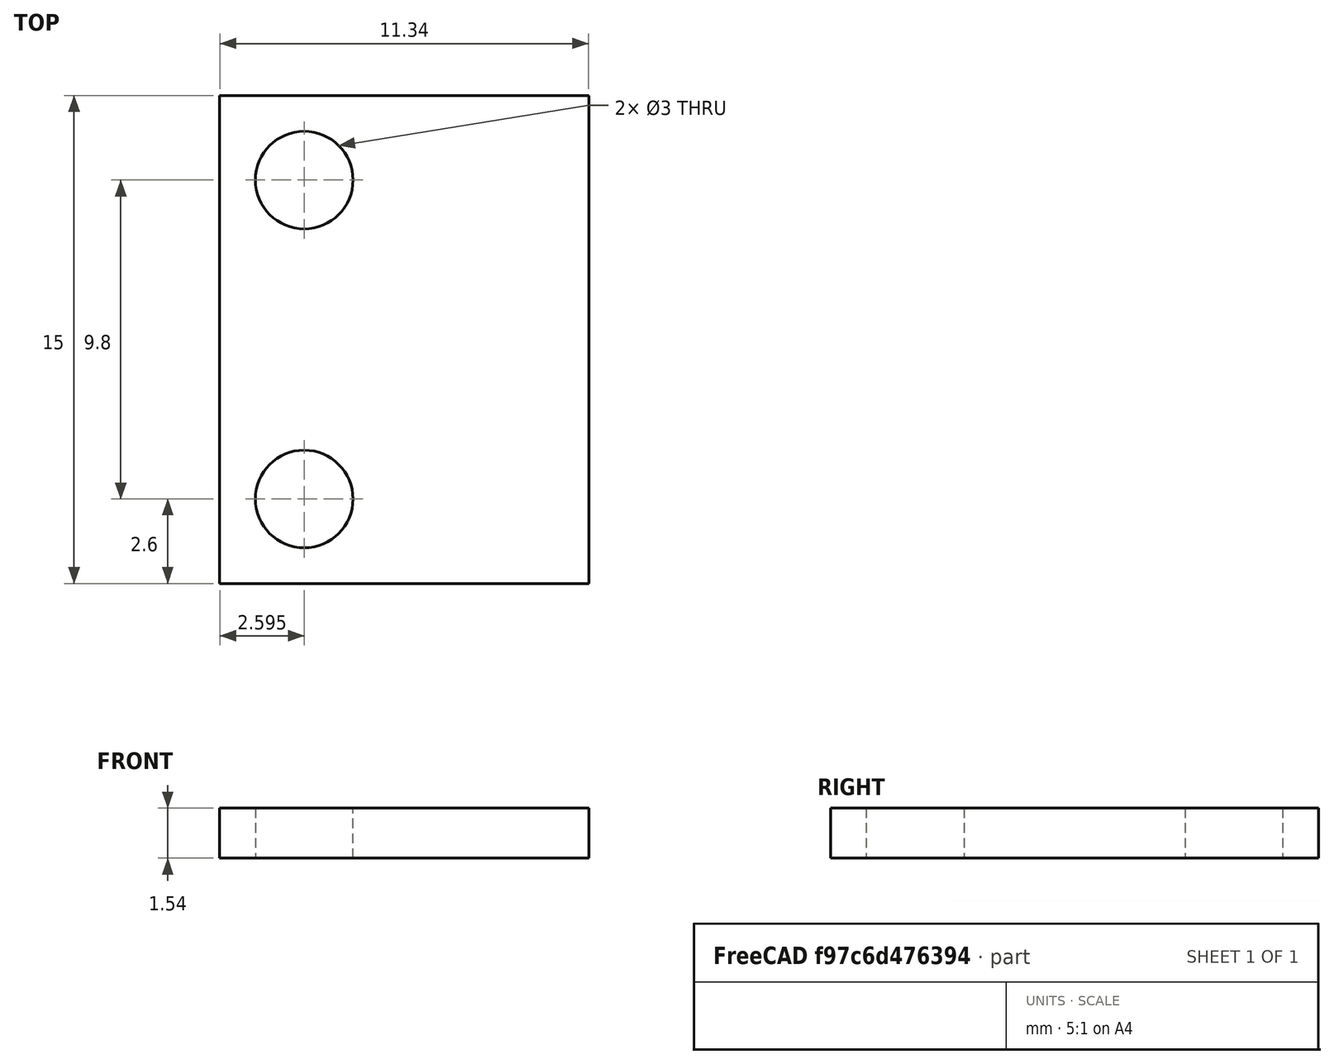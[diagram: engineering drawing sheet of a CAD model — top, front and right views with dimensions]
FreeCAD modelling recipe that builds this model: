
FCSTD DOCUMENT  (FreeCAD 0.20R29177 (Git))
Label: bme280
License: All rights reserved
LicenseURL: http://en.wikipedia.org/wiki/All_rights_reserved
objects: Sketcher::SketchObject×1, PartDesign::Pad×1, PartDesign::Body×1
note: 4 computed .brp shape members not serialized (recipe doc carries the construction recipe); baked Part::Feature solids carry a one-line shape summary decoded from their .brp

FEATURE [Sketcher::SketchObject] Sketch
  FullyConstrained = true
  expr: Constraints[13] = .Constraints.bohr_durchmesser / 2 + 1.1mm
  expr: Constraints[14] = .Constraints.bohr_durchmesser / 2 + 1.1mm
  expr: Constraints[15] = .Constraints.bohr_durchmesser / 2 + 1.1mm
  expr: Constraints[16] = .Constraints.bohr_durchmesser / 2 + 1.1mm
  sketch-geometry (6):
    g0: LineSegment StartX=-5.675 StartY=7.5 StartZ=0 EndX=5.675 EndY=7.5 EndZ=0
    g1: LineSegment StartX=5.675 StartY=7.5 StartZ=0 EndX=5.675 EndY=-7.5 EndZ=0
    g2: LineSegment StartX=5.675 StartY=-7.5 StartZ=0 EndX=-5.675 EndY=-7.5 EndZ=0
    g3: LineSegment StartX=-5.675 StartY=-7.5 StartZ=0 EndX=-5.675 EndY=7.5 EndZ=0
    g4: Circle CenterX=-3.075 CenterY=4.9 CenterZ=0 NormalX=0 NormalY=0 NormalZ=1 AngleXU=0 Radius=1.5
    g5: Circle CenterX=-3.075 CenterY=-4.9 CenterZ=0 NormalX=0 NormalY=0 NormalZ=1 AngleXU=0 Radius=1.5
  constraints (17):
    c: Coincident(g0,g1)
    c: Coincident(g1,g2)
    c: Coincident(g2,g3)
    c: Coincident(g3,g0)
    c: Horizontal(g0)
    c: Horizontal(g2)
    c: Vertical(g1)
    c: Vertical(g3)
    c: Symmetric(g2,g0,g-1)
    c: DistanceX(g0,g0) = 11.35  'breite'
    c: DistanceY(g1,g1) = 15  'hoehe'
    c: Diameter(g4) = 3  'bohr_durchmesser'
    c: Equal(g4,g5)
    c: DistanceX(g0,g4) = 2.6
    c: DistanceY(g4,g0) = 2.6
    c: DistanceY(g2,g5) = 2.6
    c: DistanceX(g2,g5) = 2.6
FEATURE [PartDesign::Pad] Pad
  Direction = (0,0,1)
  Length = 1.54
  Length2 = 10
  Profile = -> Sketch
  ReferenceAxis = -> Sketch [N_Axis]
  Type = 0
FEATURE [PartDesign::Body] Body
  Group = -> [Sketch,Pad]
  Origin = -> Origin
  Tip = -> Pad
